# Revit family: STL24908BR_30_40_STL24908PTO_30_40
name_source: partatom
category: Luminárias
units: mm (PartAtom-declared; Revit-internal decimal feet)

## family parameters
Compartilhado = Não
Corte com vazios quando carregada = Não
Cota do conector redondo = Utilizar diâmetro
Fonte luminosa = Sim
Hospedeiro = Forro
Manter orientação da anotação = Não
Número OmniClass = 23.80.70.11
Ponto de cálculo do ambiente = Não
Sempre na vertical = Sim
Tipo de parte = Normal
Título OmniClass = Luminaries for Internal Lighting

## types (4) — shared parameters
Altura = 0.06 m
Comprimento = 0.3 m
Dimerização = 20-100%
Fabricante = Stella
Filtro de cor = 16777215
Grau de proteção (IP) = IP20
IRC (Índice de reprodução de cores) = >93 (R9 >60)
Largura = 0.3 m
Modelo = S.Deep - Luminária de Embutir Super-recuada
Potência = 20 W
Tensão Elétrica = 100V-240V
Troca de temperatura da cor de lâmpada com esmaecimento = <Nenhum>
URL = https://stella.com.br
Ângulo de Abertura = 85°
Ângulo de inclinação = 90.00°
zero-valued in all types: Elevação padrão

## per-type parameters (varying)
| type | Arquivo de rede fotométrica | Estrutura | Fluxo Luminoso | Luminoso | Referência | Temperatura da cor (K) |
| STL24908BR/30 - BIVOLT - 3000K - 1600lm - 85° | STELLA - STL24908BR-30 - PAINEL DE EMBUTIR SUPER RECUADO S.DEEP 20W.ies | Al - Branco | 1600 lm | Luminoso - 3000K | STL24908BR/30 - BIVOLT | 3000 K |
| STL24908BR/40 - BIVOLT - 4000K - 1700lm - 85° | STELLA - STL24908BR-40 - PAINEL DE EMBUTIR SUPER RECUADO S.DEEP 20W.ies | Al - Branco | 1700 lm | Luminoso - 4000K | STL24908BR/40 - BIVOLT | 4000 K |
| STL24908PTO/30 - BIVOLT - 3000K - 1100lm - 85° | STELLA - STL24908PTO-30 - PAINEL DE EMBUTIR SUPER RECUADO S.DEEP 20W.ies | Al - Preto | 1100 lm | Luminoso - 3000K | STL24908PTO/30 - BIVOLT | 3000 K |
| STL24908PTO/40 - BIVOLT - 4000K - 1200lm - 85° | STELLA - STL24908PTO-40 - PAINEL DE EMBUTIR SUPER RECUADO S.DEEP 20W.ies | Al - Preto | 1200 lm | Luminoso - 4000K | STL24908PTO/40 - BIVOLT | 4000 K |
